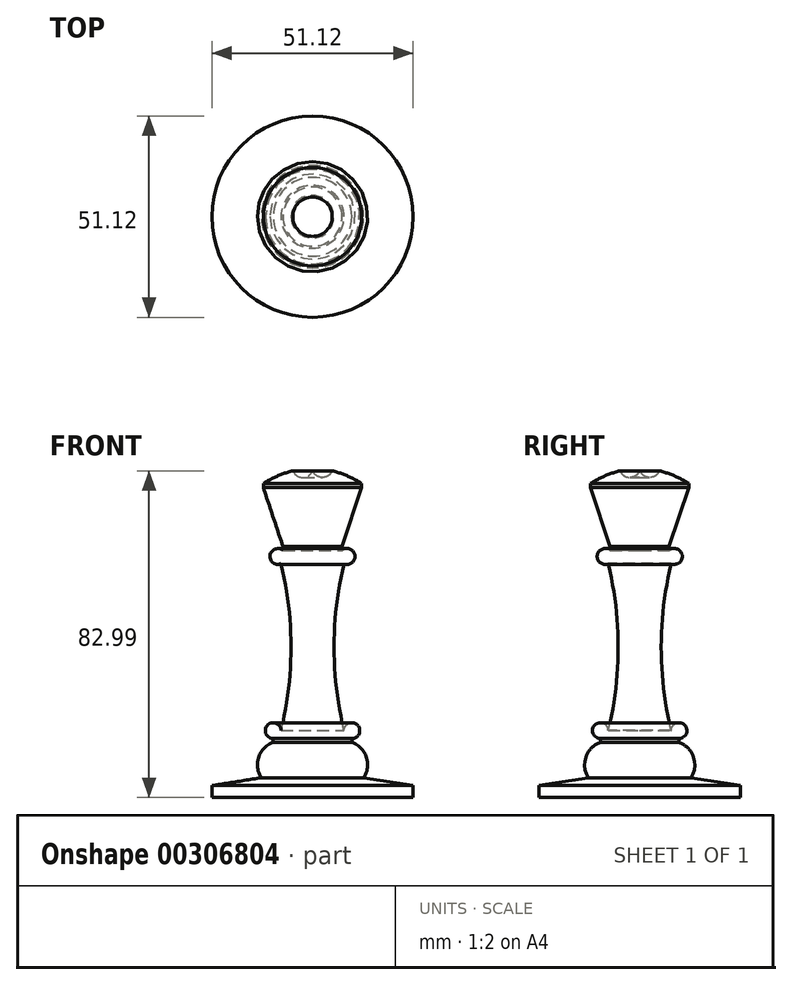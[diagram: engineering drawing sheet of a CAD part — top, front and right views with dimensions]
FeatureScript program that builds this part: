
annotation { "Feature Type Name" : "Feature", "Feature Type Description" : "" }
export const myFeature = defineFeature(function(context is Context, id is Id, definition is map)
    precondition{}
    {
        {
            var Q0;
            Q0=qCreatedBy(makeId("Front.planeOp"),FACE);
            var sketch = newSketch(context, id + "F0", { "sketchPlane" : qUnion([Q0])});
            skArc(sketch, "E0", {"start": v(5, -2) * mm, "mid": v(3.5, 1.5) * mm, "end": v(0, 0) * mm});
            skArc(sketch, "E1", {"start": v(12.5, -5.27) * mm, "mid": v(8.88, -3.33) * mm, "end": v(5, -2) * mm});
            skLineSegment(sketch, "E2", {"start": v(12.5, -5.27) * mm, "end": v(12.5, -6.27) * mm});
            skLineSegment(sketch, "E3", {"start": v(12.5, -6.27) * mm, "end": v(7.5, -21.27) * mm});
            skLineSegment(sketch, "E4", {"start": v(7.5, -21.27) * mm, "end": v(7.5, -22.27) * mm});
            skArc(sketch, "E5", {"start": v(8, -25.59) * mm, "mid": v(10.8, -23.47) * mm, "end": v(7.5, -22.27) * mm});
            skArc(sketch, "E6", {"start": v(8, -25.6) * mm, "mid": v(5.46, -46.8) * mm, "end": v(8, -68.02) * mm});
            skArc(sketch, "E7", {"start": v(10, -70.02) * mm, "mid": v(11.41, -66.6) * mm, "end": v(8, -68.02) * mm});
            skLineSegment(sketch, "E8", {"start": v(10, -70.02) * mm, "end": v(10, -71.02) * mm});
            skArc(sketch, "E9", {"start": v(13, -80) * mm, "mid": v(13.69, -74.77) * mm, "end": v(10, -71.02) * mm});
            skLineSegment(sketch, "E10", {"start": v(13, -80) * mm, "end": v(25.56, -82) * mm});
            skLineSegment(sketch, "E11", {"start": v(25.56, -82) * mm, "end": v(25.56, -85) * mm});
            skLineSegment(sketch, "E12", {"start": v(25.56, -85) * mm, "end": v(0, -85) * mm});
            skLineSegment(sketch, "E13", {"start": v(0, -85) * mm, "end": v(0, 0) * mm});
            skSolve(sketch);
        }
        {
            var Q0;
            Q0 = qSketchRegion(id + "F0", true);
            var Q1;
            Q1=sQuery(id+"F0.wireOp",EDGE,"E13");
            revolve(context, id + "F1", {"entities" : qUnion([Q0]), "axis" : qUnion([Q1]), "revolveType" : RevolveType.FULL});
        }
    });
